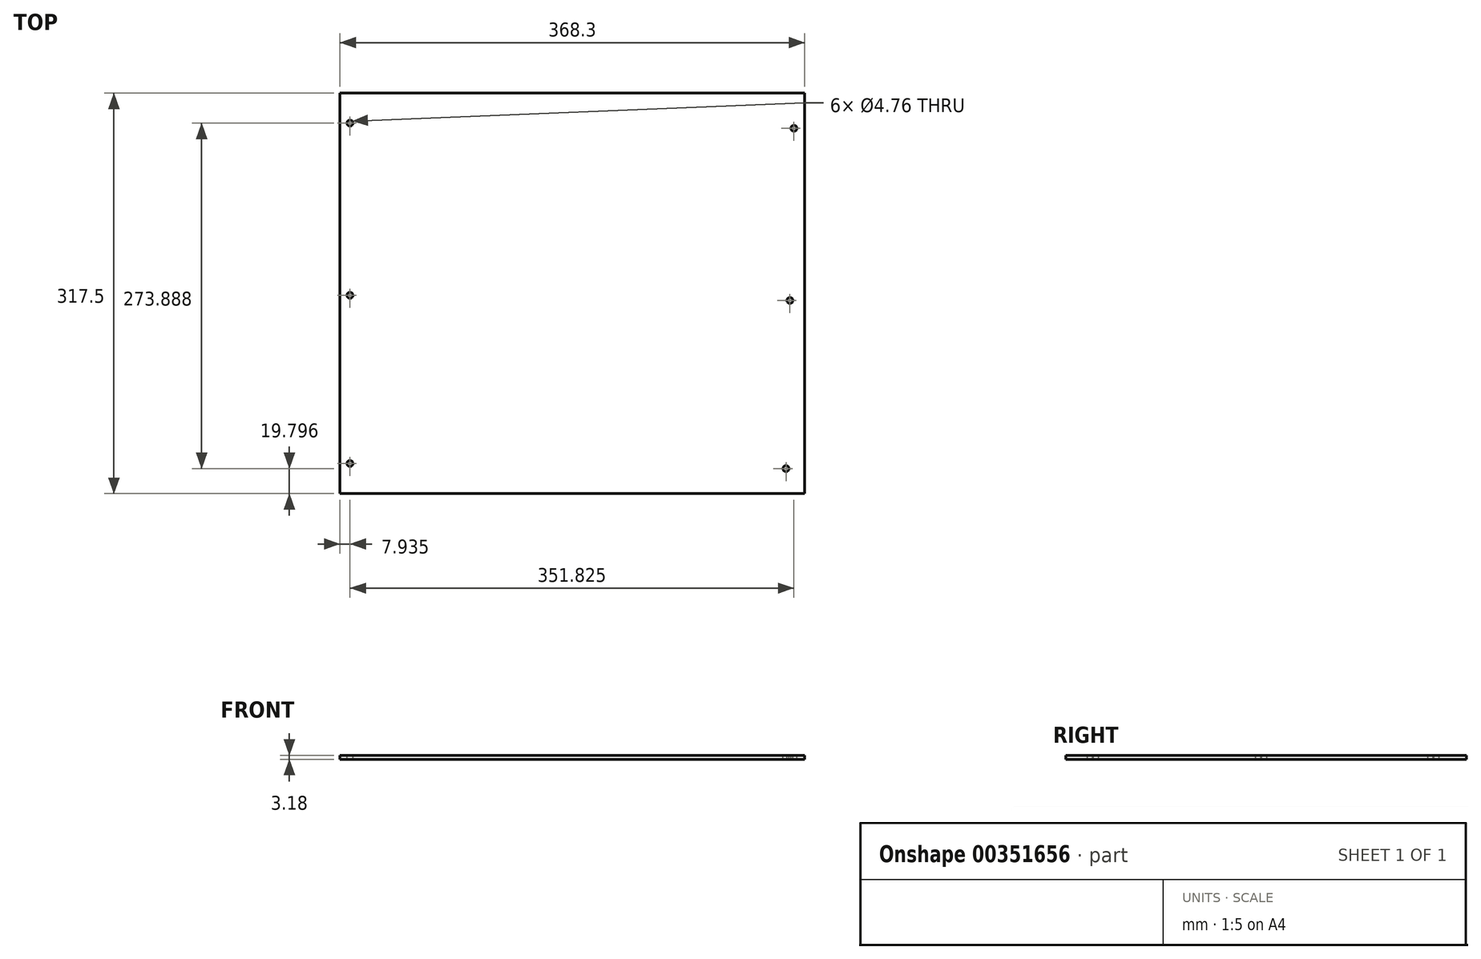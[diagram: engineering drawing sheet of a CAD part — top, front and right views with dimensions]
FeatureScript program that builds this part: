
annotation { "Feature Type Name" : "Feature", "Feature Type Description" : "" }
export const myFeature = defineFeature(function(context is Context, id is Id, definition is map)
    precondition{}
    {
        {
            var Q0;
            Q0=qCreatedBy(makeId("Top.planeOp"),FACE);
            var sketch = newSketch(context, id + "F0", { "sketchPlane" : qUnion([Q0])});
            skLineSegment(sketch, "E0.bottom", {"start": v(-180.46, 95.88) * mm, "end": v(187.84, 95.88) * mm});
            skLineSegment(sketch, "E0.top", {"start": v(-180.46, -221.62) * mm, "end": v(187.84, -221.62) * mm});
            skLineSegment(sketch, "E0.left", {"start": v(-180.46, 95.88) * mm, "end": v(-180.46, -221.62) * mm});
            skLineSegment(sketch, "E0.right", {"start": v(187.84, 95.88) * mm, "end": v(187.84, -221.62) * mm});
            skSolve(sketch);
        }
        {
            var Q0;
            Q0 = qSketchRegion(id + "F0", true);
            extrude(context, id + "F1", {"entities" : qUnion([Q0]), "depth" : 3.17 * mm});
        }
        {
            var Q0;
            Q0=makeQuery(id+"F1.opExtrude","CAP_FACE",FACE,{"disambiguationData":[OSD([sQuery(id+"F0.wireOp",EDGE,"E0.bottom"),sQuery(id+"F0.wireOp",EDGE,"E0.top"),sQuery(id+"F0.wireOp",EDGE,"E0.left"),sQuery(id+"F0.wireOp",EDGE,"E0.right")])],"isStart":false});
            var sketch = newSketch(context, id + "F2", { "sketchPlane" : qUnion([Q0])});
            skCircle(sketch, "E1", {"center": v(-172.53, -197.81) * mm, "radius": 2.38 * mm});
            skCircle(sketch, "E2", {"center": v(-172.53, -64.46) * mm, "radius": 2.38 * mm});
            skCircle(sketch, "E3", {"center": v(-172.53, 72.06) * mm, "radius": 2.38 * mm});
            skLineSegment(sketch, "E4", {"start": v(3.69, 95.88) * mm, "end": v(0, -221.62) * mm, "construction": true});
            skPoint(sketch, "E4.endSnap0", {"position": v(3.69, -221.62) * mm});
            skCircle(sketch, "E5.MirrorC", {"center": v(173.03, -201.82) * mm, "radius": 2.38 * mm});
            skCircle(sketch, "E6.MirrorC", {"center": v(176.13, -68.5) * mm, "radius": 2.38 * mm});
            skCircle(sketch, "E7.MirrorC", {"center": v(179.3, 67.98) * mm, "radius": 2.38 * mm});
            skSolve(sketch);
        }
        {
            var Q0;
            Q0 = qSketchRegion(id + "F2", true);
            extrude(context, id + "F3", {"entities" : qUnion([Q0]), "operationType" : NewBodyOperationType.REMOVE, "oppositeDirection" : true, "depth" : 25.4 * mm});
        }
    });
